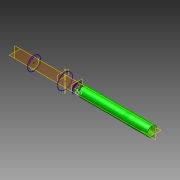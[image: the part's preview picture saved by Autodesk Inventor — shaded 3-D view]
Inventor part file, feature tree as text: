
AUTODESK INVENTOR PART (.ipt)
format: ipt  version: 2015 (Build 190159000, 159)  size: 278,016 bytes
history: native  units: in
note: dims shown in document units (in); Inventor stores cm internally (conversion verified against a paired STEP export)
features: extrude x9, sketch x9, revolve x3, hole x2, plane x2, mirror x1, pattern_circular x1
ambient origin geometry x8: Origin, YZ Plane, XZ Plane, XY Plane, X Axis, Y Axis, Z Axis, Center Point
bodies: Solid1 (feature_tree)
feature tree (27):
  revolve  "Revolution1"  [1 undecoded]
  extrude  "Extrusion1"  Depth=0.29in
  hole  "Hole1"  [1 undecoded]
  hole  "Hole2"  [1 undecoded]
  sketch  "Sketch3"  dims[d4=0.3in d5=0.1in]
  extrude  "Extrusion2"  Depth=0.3in
  extrude  "Extrusion3"  Depth=0.05in
  extrude  "Extrusion4"  Depth=0.04in
  mirror  "Mirror1"
  plane  "Work Plane2"
  sketch  "Sketch7"  dims[d8=0.3in d9=0.44in]
  extrude  "Extrusion5"  Depth=0.2in TaperAngle=0.0deg
  extrude  "Extrusion6"  Depth=0.1in
  pattern_circular  "Circular Pattern1"  [2 undecoded]
  plane  "Work Plane3"
  extrude  "Extrusion7"  Depth=0.1in TaperAngle=0.0deg
  sketch  "Sketch9"  dims[d12=90.0deg d13=0.04in]
  extrude  "Extrusion8"  Depth=0.1in TaperAngle=0.0deg
  extrude  "Extrusion9"  [1 undecoded]
  revolve  "Revolution2"  [1 undecoded]
  revolve  "Revolution3"  [1 undecoded]
  sketch  "Sketch1"  dims[d0=0.07in d1=0.4in]
  sketch  "Sketch2"  dims[d2=0.365in d3=0.29in]
  sketch  "Sketch4"  dims[d6=0.06in d7=0.3in]
  sketch  "Sketch8"  dims[d10=0.28in d11=0.05in]
  sketch  "Sketch10"  dims[d14=0.2in d15=1.0in d16=0.0in]
  sketch  "Sketch11"  dims[d17=1.0in d18=1.0in d19=0.1875in d20=0.75in d21=0.25in d22=0.25in d23=0.5635in d24=0.4375in d25=0.0in d26=1.0in d27=1.0in d28=0.1875in d29=0.75in d30=0.25in d31=0.05in d32=0.5635in d33=0.375in d34=0.0in d35=0.07in d36=0.0in d37=0.085in d38=0.0in d39=1.15in d40=0.0in d42=-1.44in d43=0.45in d44=0.025in d45=0.025in d46=0.01in d47=0.03in d48=0.05in d49=0.0in d50=0.05in d51=0.0in d52=5.1181in d53=360.0deg d55=-1.8in d56=1.8in d57=0.0in d58=0.02in d59=0.4in d60=0.0in d61=0.2in d62=0.0in d63=0.2in d64=0.4466in d65=0.1in d66=30.0deg]
note: 8 required parameter values undecoded (feature->parameter linkage not recoverable at this tier; creation-order binding heuristic only, values carry confidence <= 0.55)